# Revit family: 706570001_Barra De Seguridad 30 Pulg
name_source: partatom
category: Plumbing Fixtures
units: mm (PartAtom-declared; Revit-internal decimal feet)

## family parameters
Always vertical = Yes
Cut with Voids When Loaded = No
Host = Wall
OmniClass Number = 23.31.00.00
OmniClass Title = Plumbing Specific Products and Equipment
Part Type = Normal
Room Calculation Point = No
Round Connector Dimension = Use Diameter
Shared = No

## types (1)
- Barra De Seguridad 30"
    Creado por = BIMBAU
    Cuidado Y Limpieza = Para prolongar y preservar las cualidades del acero es vital que la limpieza profunda del producto se haga únicamente con agua y jabón suave y que en el secado y el brillo se utilice un paño de algodón limpio, dicha limpieza se recomienda 2 veces a la semana, y en zonas costeras a diario por la salinidad del ambiente. Por ningún motivo deben usarse elementos abrasivos, ácidos o disolventes para la limpieza del producto. (ácido muriático, ácido sulfúrico, yodo, derivados del cloro, amoniaco, blanqueadores.) Los acabados pueden variar su comportamiento en zonas costeras y/o en ambientes corrosivos. En referencias satinadas limpie en el sentido del pulido del acero.
    Default Elevation = 0 mm  [stored 0 ft]
    Description = Barra en acero inoxidable 304. Con tornillos de anclaje en acero inoxidable 
para evitar la corrosión. Con escudos protectores que cubren los tonillos. 
Elemento de mobiliario para el apoyo, seguridad y protección de usuarios 
que acompaña la dirección de una circulación.
    Fecha de creación = 12/04/2021
    Longitud = 762 mm  [stored 2.5 ft]
    Manufacturer = Corona
    Material = Corona_Acabado_Satinado
    Model = Barra de seguridad 30P
    Profundidad = 78.8 mm  [stored 0.25853 ft]
    Recubrimientos = -Material: Acero inoxidable SUS 304. -Resistente a la corrosión, pelado y decoloración por agua. -Condición de servicio recomendada, uso doméstico e institucional.
    Referencia = 706570001
    Soporte de carga = 200 Kg.
    URL = https://corona.co

note: [stored X ft] marks values corroborated as IEEE doubles in the binary element streams (Revit-internal decimal feet)

## geometry (parser evidence)
native form markers: Sweep x3
no freeform markers — native parametric forms only
